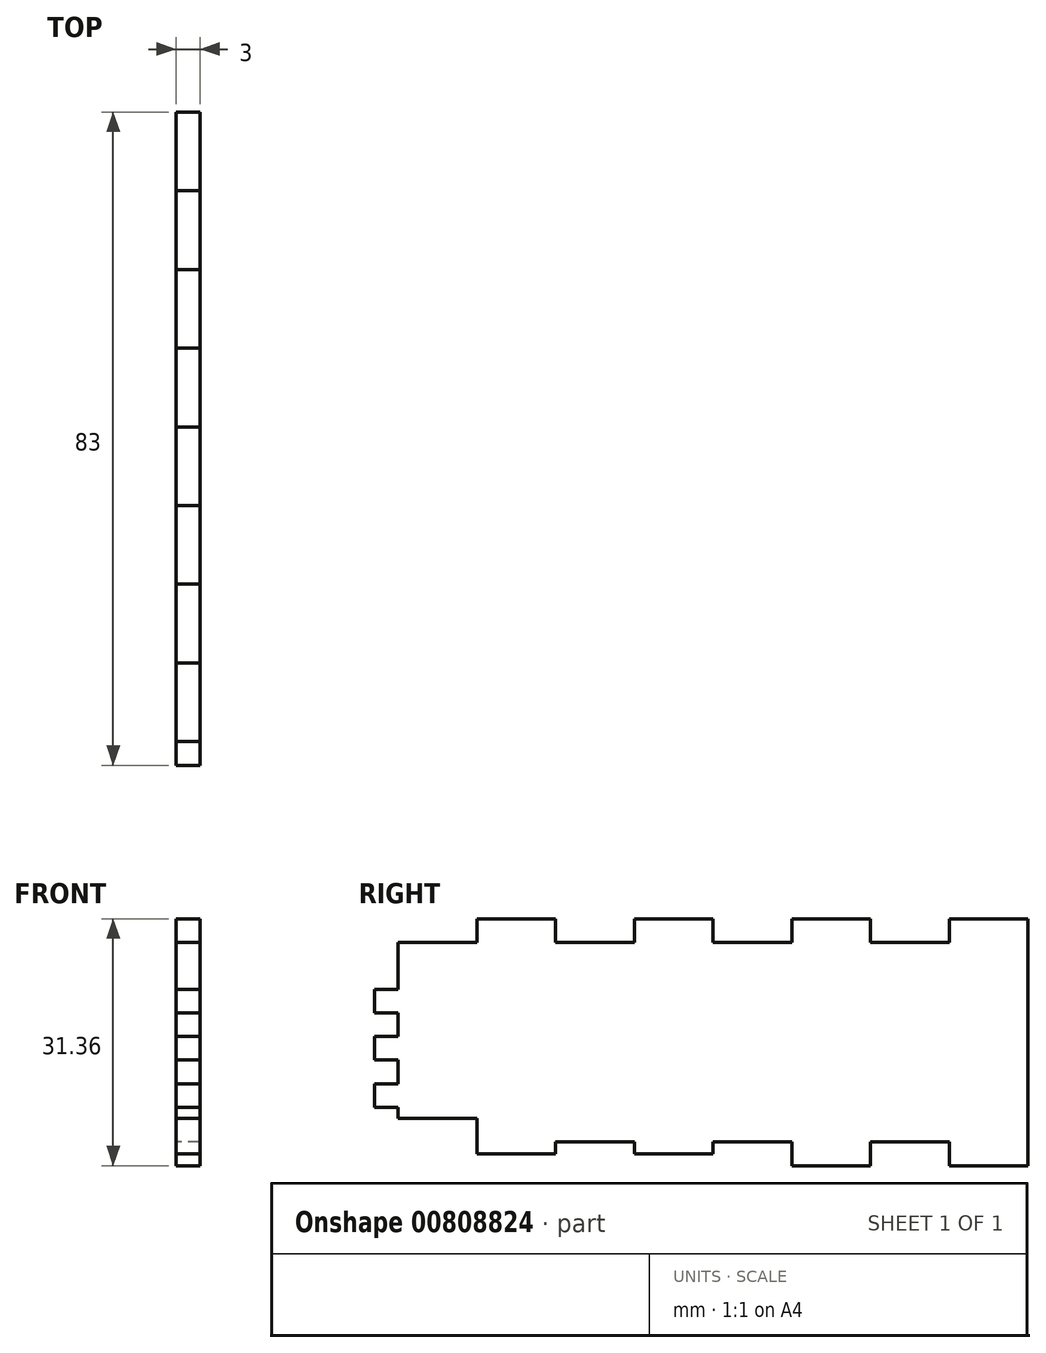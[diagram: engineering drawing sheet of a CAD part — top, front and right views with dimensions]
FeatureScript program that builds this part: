
annotation { "Feature Type Name" : "Feature", "Feature Type Description" : "" }
export const myFeature = defineFeature(function(context is Context, id is Id, definition is map)
    precondition{}
    {
        {
            var Q0;
            Q0=qCreatedBy(makeId("Right.planeOp"),FACE);
            var sketch = newSketch(context, id + "F0", { "sketchPlane" : qUnion([Q0])});
            skLineSegment(sketch, "E0.bottom", {"start": v(-40, 11.18) * mm, "end": v(40, 11.18) * mm});
            skLineSegment(sketch, "E0.top", {"start": v(-40, -11.18) * mm, "end": v(40, -11.18) * mm});
            skLineSegment(sketch, "E0.left", {"start": v(-40, 11.18) * mm, "end": v(-40, -11.18) * mm});
            skLineSegment(sketch, "E0.right", {"start": v(40, 11.18) * mm, "end": v(40, -11.18) * mm});
            skPoint(sketch, "E0.middle", {"position": v(0, 0) * mm});
            skLineSegment(sketch, "E1.bottom", {"start": v(-40, 5.23) * mm, "end": v(-43, 5.23) * mm});
            skLineSegment(sketch, "E1.top", {"start": v(-40, 2.23) * mm, "end": v(-43, 2.23) * mm});
            skLineSegment(sketch, "E1.left", {"start": v(-40, 5.23) * mm, "end": v(-40, 2.23) * mm});
            skLineSegment(sketch, "E1.right", {"start": v(-43, 5.23) * mm, "end": v(-43, 2.23) * mm});
            skLineSegment(sketch, "E2.bottom", {"start": v(-40, -0.77) * mm, "end": v(-43, -0.77) * mm});
            skLineSegment(sketch, "E2.top", {"start": v(-40, -3.77) * mm, "end": v(-43, -3.77) * mm});
            skLineSegment(sketch, "E2.left", {"start": v(-40, -0.77) * mm, "end": v(-40, -3.77) * mm});
            skLineSegment(sketch, "E2.right", {"start": v(-43, -0.77) * mm, "end": v(-43, -3.77) * mm});
            skLineSegment(sketch, "E3.bottom", {"start": v(-40, -6.77) * mm, "end": v(-43, -6.77) * mm});
            skLineSegment(sketch, "E3.top", {"start": v(-40, -9.77) * mm, "end": v(-43, -9.77) * mm});
            skLineSegment(sketch, "E3.left", {"start": v(-40, -6.77) * mm, "end": v(-40, -9.77) * mm});
            skLineSegment(sketch, "E3.right", {"start": v(-43, -6.77) * mm, "end": v(-43, -9.77) * mm});
            skLineSegment(sketch, "E4.bottom", {"start": v(-40, -11.18) * mm, "end": v(-30, -11.18) * mm});
            skLineSegment(sketch, "E4.top", {"start": v(-40, -14.18) * mm, "end": v(-30, -14.18) * mm});
            skLineSegment(sketch, "E4.left", {"start": v(-40, -11.18) * mm, "end": v(-40, -14.18) * mm});
            skLineSegment(sketch, "E4.right", {"start": v(-30, -11.18) * mm, "end": v(-30, -14.18) * mm});
            skLineSegment(sketch, "E5.bottom", {"start": v(-40, 11.18) * mm, "end": v(-30, 11.18) * mm});
            skLineSegment(sketch, "E5.top", {"start": v(-40, 14.18) * mm, "end": v(-30, 14.18) * mm});
            skLineSegment(sketch, "E5.left", {"start": v(-40, 11.18) * mm, "end": v(-40, 14.18) * mm});
            skLineSegment(sketch, "E5.right", {"start": v(-30, 11.18) * mm, "end": v(-30, 14.18) * mm});
            skLineSegment(sketch, "E6.1.0.0", {"start": v(-20, 11.18) * mm, "end": v(-20, 14.18) * mm});
            skLineSegment(sketch, "E6.1.0.1", {"start": v(-30, 14.18) * mm, "end": v(-20, 14.18) * mm});
            skLineSegment(sketch, "E6.1.0.3", {"start": v(-20, -11.18) * mm, "end": v(-20, -14.18) * mm});
            skLineSegment(sketch, "E6.1.0.4", {"start": v(-30, -14.18) * mm, "end": v(-20, -14.18) * mm});
            skLineSegment(sketch, "E6.2.0.0", {"start": v(-10, 11.18) * mm, "end": v(-10, 14.18) * mm});
            skLineSegment(sketch, "E6.2.0.1", {"start": v(-20, 14.18) * mm, "end": v(-10, 14.18) * mm});
            skLineSegment(sketch, "E6.2.0.2", {"start": v(-20, 11.18) * mm, "end": v(-20, 14.18) * mm});
            skLineSegment(sketch, "E6.2.0.3", {"start": v(-10, -11.18) * mm, "end": v(-10, -14.18) * mm});
            skLineSegment(sketch, "E6.2.0.4", {"start": v(-20, -14.18) * mm, "end": v(-10, -14.18) * mm});
            skLineSegment(sketch, "E6.2.0.5", {"start": v(-20, -11.18) * mm, "end": v(-20, -14.18) * mm});
            skLineSegment(sketch, "E6.3.0.0", {"start": v(0, 11.18) * mm, "end": v(0, 14.18) * mm});
            skLineSegment(sketch, "E6.3.0.1", {"start": v(-10, 14.18) * mm, "end": v(0, 14.18) * mm});
            skLineSegment(sketch, "E6.3.0.2", {"start": v(-10, 11.18) * mm, "end": v(-10, 14.18) * mm});
            skLineSegment(sketch, "E6.3.0.3", {"start": v(0, -11.18) * mm, "end": v(0, -14.18) * mm});
            skLineSegment(sketch, "E6.3.0.4", {"start": v(-10, -14.18) * mm, "end": v(0, -14.18) * mm});
            skLineSegment(sketch, "E6.3.0.5", {"start": v(-10, -11.18) * mm, "end": v(-10, -14.18) * mm});
            skLineSegment(sketch, "E6.4.0.0", {"start": v(10, 11.18) * mm, "end": v(10, 14.18) * mm});
            skLineSegment(sketch, "E6.4.0.1", {"start": v(0, 14.18) * mm, "end": v(10, 14.18) * mm});
            skLineSegment(sketch, "E6.4.0.2", {"start": v(0, 11.18) * mm, "end": v(0, 14.18) * mm});
            skLineSegment(sketch, "E6.4.0.3", {"start": v(10, -11.18) * mm, "end": v(10, -14.18) * mm});
            skLineSegment(sketch, "E6.4.0.4", {"start": v(0, -14.18) * mm, "end": v(10, -14.18) * mm});
            skLineSegment(sketch, "E6.4.0.5", {"start": v(0, -11.18) * mm, "end": v(0, -14.18) * mm});
            skLineSegment(sketch, "E6.5.0.0", {"start": v(20, 11.18) * mm, "end": v(20, 14.18) * mm});
            skLineSegment(sketch, "E6.5.0.1", {"start": v(10, 14.18) * mm, "end": v(20, 14.18) * mm});
            skLineSegment(sketch, "E6.5.0.2", {"start": v(10, 11.18) * mm, "end": v(10, 14.18) * mm});
            skLineSegment(sketch, "E6.5.0.3", {"start": v(20, -11.18) * mm, "end": v(20, -14.18) * mm});
            skLineSegment(sketch, "E6.5.0.4", {"start": v(10, -14.18) * mm, "end": v(20, -14.18) * mm});
            skLineSegment(sketch, "E6.5.0.5", {"start": v(10, -11.18) * mm, "end": v(10, -14.18) * mm});
            skLineSegment(sketch, "E6.6.0.0", {"start": v(30, 11.18) * mm, "end": v(30, 14.18) * mm});
            skLineSegment(sketch, "E6.6.0.1", {"start": v(20, 14.18) * mm, "end": v(30, 14.18) * mm});
            skLineSegment(sketch, "E6.6.0.2", {"start": v(20, 11.18) * mm, "end": v(20, 14.18) * mm});
            skLineSegment(sketch, "E6.6.0.3", {"start": v(30, -11.18) * mm, "end": v(30, -14.18) * mm});
            skLineSegment(sketch, "E6.6.0.4", {"start": v(20, -14.18) * mm, "end": v(30, -14.18) * mm});
            skLineSegment(sketch, "E6.6.0.5", {"start": v(20, -11.18) * mm, "end": v(20, -14.18) * mm});
            skLineSegment(sketch, "E6.7.0.0", {"start": v(40, 11.18) * mm, "end": v(40, 14.18) * mm});
            skLineSegment(sketch, "E6.7.0.1", {"start": v(30, 14.18) * mm, "end": v(40, 14.18) * mm});
            skLineSegment(sketch, "E6.7.0.2", {"start": v(30, 11.18) * mm, "end": v(30, 14.18) * mm});
            skLineSegment(sketch, "E6.7.0.3", {"start": v(40, -11.18) * mm, "end": v(40, -14.18) * mm});
            skLineSegment(sketch, "E6.7.0.4", {"start": v(30, -14.18) * mm, "end": v(40, -14.18) * mm});
            skLineSegment(sketch, "E6.7.0.5", {"start": v(30, -11.18) * mm, "end": v(30, -14.18) * mm});
            skLineSegment(sketch, "E6.direction1", {"start": v(-30, 11.18) * mm, "end": v(-20, 11.18) * mm, "construction": true});
            skLineSegment(sketch, "E7.top", {"start": v(-30, -17.18) * mm, "end": v(-20, -17.18) * mm});
            skLineSegment(sketch, "E7.left", {"start": v(-30, -14.18) * mm, "end": v(-30, -17.18) * mm});
            skLineSegment(sketch, "E7.right", {"start": v(-20, -14.18) * mm, "end": v(-20, -17.18) * mm});
            skLineSegment(sketch, "E8.1.0.0", {"start": v(0, -14.18) * mm, "end": v(0, -17.18) * mm});
            skLineSegment(sketch, "E8.1.0.1", {"start": v(-10, -17.18) * mm, "end": v(0, -17.18) * mm});
            skLineSegment(sketch, "E8.1.0.2", {"start": v(-10, -14.18) * mm, "end": v(-10, -17.18) * mm});
            skLineSegment(sketch, "E8.2.0.0", {"start": v(20, -14.18) * mm, "end": v(20, -17.18) * mm});
            skLineSegment(sketch, "E8.2.0.1", {"start": v(10, -17.18) * mm, "end": v(20, -17.18) * mm});
            skLineSegment(sketch, "E8.2.0.2", {"start": v(10, -14.18) * mm, "end": v(10, -17.18) * mm});
            skLineSegment(sketch, "E8.3.0.0", {"start": v(40, -14.18) * mm, "end": v(40, -17.18) * mm});
            skLineSegment(sketch, "E8.3.0.1", {"start": v(30, -17.18) * mm, "end": v(40, -17.18) * mm});
            skLineSegment(sketch, "E8.3.0.2", {"start": v(30, -14.18) * mm, "end": v(30, -17.18) * mm});
            skLineSegment(sketch, "E8.direction1", {"start": v(-20, -17.18) * mm, "end": v(0, -17.18) * mm, "construction": true});
            skSolve(sketch);
        }
        {
            var Q0;
            {var subQ1=sQuery(id+"F0.wireOp",EDGE,"E0.right");Q0=makeQuery(id+"F0.imprint","IMPRINT",FACE,{"disambiguationData":[TD([[makeQuery(id+"F0.imprint","IMPRINT",EDGE,{"derivedFrom":subQ1}),-1.0]])]});}
            var Q1;
            Q1=makeQuery(id+"F0.imprint","IMPRINT",FACE,{"disambiguationData":[TD([[makeQuery(id+"F0.imprint","IMPRINT",EDGE,{"derivedFrom":sQuery(id+"F0.wireOp",EDGE,"E3.bottom")}),1.0]])]});
            var Q2;
            Q2=makeQuery(id+"F0.imprint","IMPRINT",FACE,{"disambiguationData":[TD([[makeQuery(id+"F0.imprint","IMPRINT",EDGE,{"derivedFrom":sQuery(id+"F0.wireOp",EDGE,"E1.bottom")}),1.0]])]});
            var Q3;
            Q3=makeQuery(id+"F0.imprint","IMPRINT",FACE,{"disambiguationData":[TD([[makeQuery(id+"F0.imprint","IMPRINT",EDGE,{"derivedFrom":sQuery(id+"F0.wireOp",EDGE,"E6.1.0.4")}),1.0]])]});
            var Q4;
            Q4=makeQuery(id+"F0.imprint","IMPRINT",FACE,{"disambiguationData":[TD([[makeQuery(id+"F0.imprint","IMPRINT",EDGE,{"derivedFrom":sQuery(id+"F0.wireOp",EDGE,"E6.1.0.1")}),-1.0]])]});
            var Q5;
            Q5=makeQuery(id+"F0.imprint","IMPRINT",FACE,{"disambiguationData":[TD([[makeQuery(id+"F0.imprint","IMPRINT",EDGE,{"derivedFrom":sQuery(id+"F0.wireOp",EDGE,"E2.bottom")}),1.0]])]});
            var Q6;
            Q6=makeQuery(id+"F0.imprint","IMPRINT",FACE,{"disambiguationData":[TD([[makeQuery(id+"F0.imprint","IMPRINT",EDGE,{"derivedFrom":sQuery(id+"F0.wireOp",EDGE,"E6.3.0.4")}),1.0]])]});
            var Q7;
            Q7=makeQuery(id+"F0.imprint","IMPRINT",FACE,{"disambiguationData":[TD([[makeQuery(id+"F0.imprint","IMPRINT",EDGE,{"derivedFrom":sQuery(id+"F0.wireOp",EDGE,"E6.3.0.1")}),-1.0]])]});
            var Q8;
            Q8=makeQuery(id+"F0.imprint","IMPRINT",FACE,{"disambiguationData":[TD([[makeQuery(id+"F0.imprint","IMPRINT",EDGE,{"derivedFrom":sQuery(id+"F0.wireOp",EDGE,"E6.5.0.1")}),-1.0]])]});
            var Q9;
            Q9=makeQuery(id+"F0.imprint","IMPRINT",FACE,{"disambiguationData":[TD([[makeQuery(id+"F0.imprint","IMPRINT",EDGE,{"derivedFrom":sQuery(id+"F0.wireOp",EDGE,"E6.5.0.4")}),1.0]])]});
            var Q10;
            {var subQ0=sQuery(id+"F0.wireOp",EDGE,"E6.7.0.0");Q10=makeQuery(id+"F0.imprint","IMPRINT",FACE,{"disambiguationData":[TD([[makeQuery(id+"F0.imprint","IMPRINT",EDGE,{"derivedFrom":subQ0}),1.0]])]});}
            var Q11;
            {var subQ0=sQuery(id+"F0.wireOp",EDGE,"E6.7.0.3");Q11=makeQuery(id+"F0.imprint","IMPRINT",FACE,{"disambiguationData":[TD([[makeQuery(id+"F0.imprint","IMPRINT",EDGE,{"derivedFrom":subQ0}),-1.0]])]});}
            var Q12;
            {var subQ0=sQuery(id+"F0.wireOp",EDGE,"E4.right");Q12=makeQuery(id+"F0.imprint","IMPRINT",FACE,{"disambiguationData":[TD([[makeQuery(id+"F0.imprint","IMPRINT",EDGE,{"derivedFrom":subQ0}),1.0]])]});}
            var Q13;
            Q13=makeQuery(id+"F0.imprint","IMPRINT",FACE,{"disambiguationData":[TD([[makeQuery(id+"F0.imprint","IMPRINT",EDGE,{"derivedFrom":sQuery(id+"F0.wireOp",EDGE,"E6.1.0.4")}),-1.0]])]});
            var Q14;
            Q14=makeQuery(id+"F0.imprint","IMPRINT",FACE,{"disambiguationData":[TD([[makeQuery(id+"F0.imprint","IMPRINT",EDGE,{"derivedFrom":sQuery(id+"F0.wireOp",EDGE,"E6.3.0.4")}),-1.0]])]});
            var Q15;
            Q15=makeQuery(id+"F0.imprint","IMPRINT",FACE,{"disambiguationData":[TD([[makeQuery(id+"F0.imprint","IMPRINT",EDGE,{"derivedFrom":sQuery(id+"F0.wireOp",EDGE,"E6.5.0.4")}),-1.0]])]});
            var Q16;
            Q16=makeQuery(id+"F0.imprint","IMPRINT",FACE,{"disambiguationData":[TD([[makeQuery(id+"F0.imprint","IMPRINT",EDGE,{"derivedFrom":sQuery(id+"F0.wireOp",EDGE,"E6.7.0.4")}),-1.0]])]});
            var Q17;
            Q17=makeQuery(id+"F0.imprint","IMPRINT",FACE,{"disambiguationData":[TD([[makeQuery(id+"F0.imprint","IMPRINT",EDGE,{"derivedFrom":sQuery(id+"F0.wireOp",EDGE,"E4.bottom")}),-1.0]])]});
            var Q18;
            Q18=makeQuery(id+"F0.imprint","IMPRINT",FACE,{"disambiguationData":[TD([[makeQuery(id+"F0.imprint","IMPRINT",EDGE,{"derivedFrom":sQuery(id+"F0.wireOp",EDGE,"E6.2.0.4")}),1.0]])]});
            var Q19;
            Q19=makeQuery(id+"F0.imprint","IMPRINT",FACE,{"disambiguationData":[TD([[makeQuery(id+"F0.imprint","IMPRINT",EDGE,{"derivedFrom":sQuery(id+"F0.wireOp",EDGE,"E6.4.0.4")}),1.0]])]});
            var Q20;
            Q20=makeQuery(id+"F0.imprint","IMPRINT",FACE,{"disambiguationData":[TD([[makeQuery(id+"F0.imprint","IMPRINT",EDGE,{"derivedFrom":sQuery(id+"F0.wireOp",EDGE,"E6.6.0.4")}),1.0]])]});
            extrude(context, id + "F1", {"entities" : qUnion([Q0, Q1, Q2, Q3, Q4, Q5, Q6, Q7, Q8, Q9, Q10, Q11, Q12, Q13, Q14, Q15, Q16, Q17, Q18, Q19, Q20]), "depth" : 3 * mm, "offsetDistance" : 25 * mm});
        }
        {
            var Q0;
            Q0=makeQuery(id+"F1.opExtrude","CAP_FACE",FACE,{"disambiguationData":[OSD([sQuery(id+"F0.wireOp",EDGE,"E0.bottom"),sQuery(id+"F0.wireOp",EDGE,"E0.left"),sQuery(id+"F0.wireOp",EDGE,"E0.right"),sQuery(id+"F0.wireOp",EDGE,"E1.bottom"),sQuery(id+"F0.wireOp",EDGE,"E1.top"),sQuery(id+"F0.wireOp",EDGE,"E1.right"),sQuery(id+"F0.wireOp",EDGE,"E2.bottom"),sQuery(id+"F0.wireOp",EDGE,"E2.top"),sQuery(id+"F0.wireOp",EDGE,"E2.right"),sQuery(id+"F0.wireOp",EDGE,"E3.bottom"),sQuery(id+"F0.wireOp",EDGE,"E3.top"),sQuery(id+"F0.wireOp",EDGE,"E3.right"),sQuery(id+"F0.wireOp",EDGE,"E4.top"),sQuery(id+"F0.wireOp",EDGE,"E4.left"),sQuery(id+"F0.wireOp",EDGE,"E5.bottom"),sQuery(id+"F0.wireOp",EDGE,"E6.1.0.1"),sQuery(id+"F0.wireOp",EDGE,"E5.right"),sQuery(id+"F0.wireOp",EDGE,"E6.2.0.2"),sQuery(id+"F0.wireOp",EDGE,"E6.2.0.4"),sQuery(id+"F0.wireOp",EDGE,"E6.3.0.1"),sQuery(id+"F0.wireOp",EDGE,"E6.3.0.2"),sQuery(id+"F0.wireOp",EDGE,"E6.4.0.2"),sQuery(id+"F0.wireOp",EDGE,"E6.4.0.4"),sQuery(id+"F0.wireOp",EDGE,"E6.5.0.1"),sQuery(id+"F0.wireOp",EDGE,"E6.5.0.2"),sQuery(id+"F0.wireOp",EDGE,"E6.6.0.2"),sQuery(id+"F0.wireOp",EDGE,"E6.6.0.4"),sQuery(id+"F0.wireOp",EDGE,"E6.7.0.0"),sQuery(id+"F0.wireOp",EDGE,"E6.7.0.1"),sQuery(id+"F0.wireOp",EDGE,"E6.7.0.2"),sQuery(id+"F0.wireOp",EDGE,"E6.7.0.3"),sQuery(id+"F0.wireOp",EDGE,"E7.top"),sQuery(id+"F0.wireOp",EDGE,"E7.left"),sQuery(id+"F0.wireOp",EDGE,"E7.right"),sQuery(id+"F0.wireOp",EDGE,"E8.1.0.0"),sQuery(id+"F0.wireOp",EDGE,"E8.1.0.1"),sQuery(id+"F0.wireOp",EDGE,"E8.1.0.2"),sQuery(id+"F0.wireOp",EDGE,"E8.2.0.0"),sQuery(id+"F0.wireOp",EDGE,"E8.2.0.1"),sQuery(id+"F0.wireOp",EDGE,"E8.2.0.2"),sQuery(id+"F0.wireOp",EDGE,"E8.3.0.0"),sQuery(id+"F0.wireOp",EDGE,"E8.3.0.1"),sQuery(id+"F0.wireOp",EDGE,"E8.3.0.2")])],"isStart":false});
            var sketch = newSketch(context, id + "F2", { "sketchPlane" : qUnion([Q0])});
            skLineSegment(sketch, "E9.bottom", {"start": v(-30, -17.18) * mm, "end": v(-20, -17.18) * mm});
            skLineSegment(sketch, "E9.top", {"start": v(-30, -15.68) * mm, "end": v(-20, -15.68) * mm});
            skLineSegment(sketch, "E9.left", {"start": v(-30, -17.18) * mm, "end": v(-30, -15.68) * mm});
            skLineSegment(sketch, "E9.right", {"start": v(-20, -17.18) * mm, "end": v(-20, -15.68) * mm});
            skLineSegment(sketch, "E10.bottom", {"start": v(-10, -17.18) * mm, "end": v(0, -17.18) * mm});
            skLineSegment(sketch, "E10.top", {"start": v(-10, -15.68) * mm, "end": v(0, -15.68) * mm});
            skLineSegment(sketch, "E10.left", {"start": v(-10, -17.18) * mm, "end": v(-10, -15.68) * mm});
            skLineSegment(sketch, "E10.right", {"start": v(0, -17.18) * mm, "end": v(0, -15.68) * mm});
            skSolve(sketch);
        }
        {
            var Q0;
            Q0=qSketchRegion(id+"F2",true);
            extrude(context, id + "F3", {"entities" : qUnion([Q0]), "operationType" : NewBodyOperationType.REMOVE, "oppositeDirection" : true, "depth" : 25 * mm, "offsetDistance" : 25 * mm});
        }
    });
